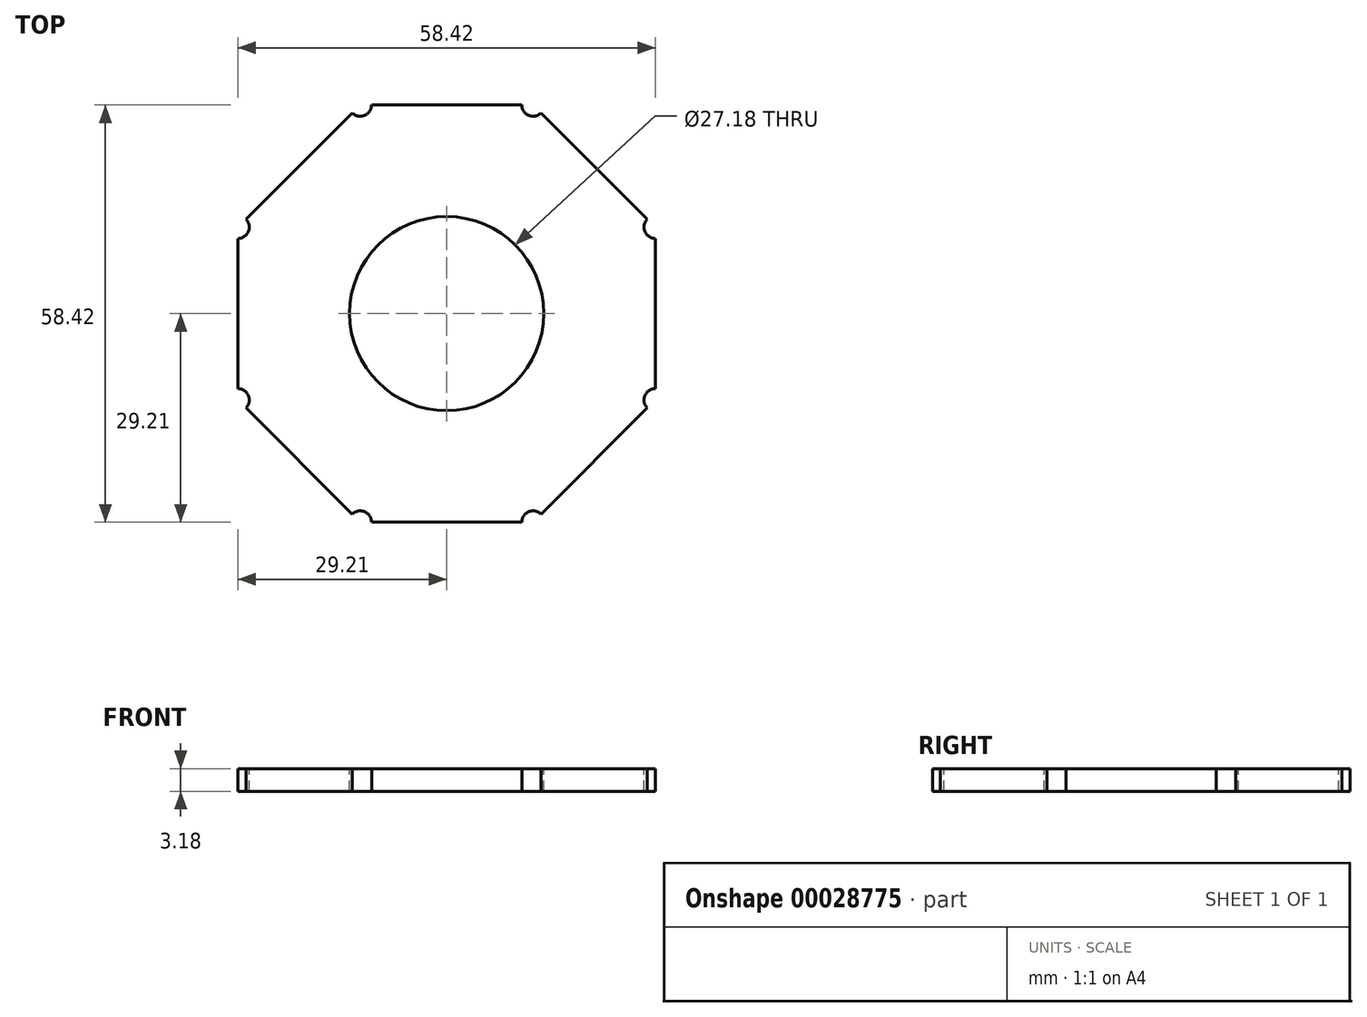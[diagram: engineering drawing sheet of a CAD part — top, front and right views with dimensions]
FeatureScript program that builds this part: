
annotation { "Feature Type Name" : "Feature", "Feature Type Description" : "" }
export const myFeature = defineFeature(function(context is Context, id is Id, definition is map)
    precondition{}
    {
        {
            var Q0;
            Q0=qCreatedBy(makeId("Top.planeOp"),FACE);
            var sketch = newSketch(context, id + "F0", { "sketchPlane" : qUnion([Q0])});
            skCircle(sketch, "E0", {"center": v(0, 0) * mm, "radius": 13.59 * mm});
            skCircle(sketch, "E1.cCircle", {"center": v(0, 0) * mm, "radius": 29.21 * mm, "construction": true});
            skLineSegment(sketch, "E1.0", {"start": v(-12.1, 29.2) * mm, "end": v(12.1, 29.2) * mm});
            skLineSegment(sketch, "E1.1", {"start": v(12.1, 29.2) * mm, "end": v(29.21, 12.1) * mm});
            skLineSegment(sketch, "E1.2", {"start": v(29.2, 12.1) * mm, "end": v(29.21, -12.1) * mm});
            skLineSegment(sketch, "E1.3", {"start": v(29.21, -12.1) * mm, "end": v(12.1, -29.2) * mm});
            skLineSegment(sketch, "E1.4", {"start": v(12.1, -29.2) * mm, "end": v(-12.1, -29.2) * mm});
            skLineSegment(sketch, "E1.5", {"start": v(-12.1, -29.21) * mm, "end": v(-29.21, -12.1) * mm});
            skLineSegment(sketch, "E1.6", {"start": v(-29.2, -12.1) * mm, "end": v(-29.2, 12.1) * mm});
            skLineSegment(sketch, "E1.7", {"start": v(-29.21, 12.1) * mm, "end": v(-12.1, 29.2) * mm});
            skPoint(sketch, "E1.0.midPoint", {"position": v(0, 29.2) * mm});
            skLineSegment(sketch, "E2", {"start": v(0, 0) * mm, "end": v(-12.1, 29.2) * mm, "construction": true});
            skLineSegment(sketch, "E3", {"start": v(0, 0) * mm, "end": v(12.1, 29.2) * mm, "construction": true});
            skLineSegment(sketch, "E4", {"start": v(0, 0) * mm, "end": v(29.21, -12.1) * mm, "construction": true});
            skLineSegment(sketch, "E5", {"start": v(0, 0) * mm, "end": v(12.1, -29.21) * mm, "construction": true});
            skLineSegment(sketch, "E6", {"start": v(0, 0) * mm, "end": v(29.2, 12.1) * mm, "construction": true});
            skLineSegment(sketch, "E7", {"start": v(0, 0) * mm, "end": v(-12.1, -29.2) * mm, "construction": true});
            skLineSegment(sketch, "E8", {"start": v(0, 0) * mm, "end": v(-29.21, -12.1) * mm});
            skLineSegment(sketch, "E9", {"start": v(0, 0) * mm, "end": v(-29.21, 12.1) * mm, "construction": true});
            skCircle(sketch, "E10", {"center": v(-12.1, 29.2) * mm, "radius": 1.59 * mm});
            skCircle(sketch, "E11", {"center": v(12.1, 29.2) * mm, "radius": 1.59 * mm});
            skCircle(sketch, "E12", {"center": v(29.2, 12.1) * mm, "radius": 1.59 * mm});
            skCircle(sketch, "E13", {"center": v(29.21, -12.1) * mm, "radius": 1.59 * mm});
            skCircle(sketch, "E14", {"center": v(12.1, -29.2) * mm, "radius": 1.59 * mm});
            skCircle(sketch, "E15", {"center": v(-12.1, -29.2) * mm, "radius": 1.59 * mm});
            skCircle(sketch, "E16", {"center": v(-29.21, -12.1) * mm, "radius": 1.59 * mm});
            skCircle(sketch, "E17", {"center": v(-29.2, 12.1) * mm, "radius": 1.59 * mm});
            skLineSegment(sketch, "E18", {"start": v(-29.21, -12.1) * mm, "end": v(-38.5, 10.35) * mm, "construction": true});
            skSolve(sketch);
        }
        {
            var Q0;
            Q0=makeQuery(id+"F0.imprint","IMPRINT",FACE,{"disambiguationData":[TD([[makeQuery(id+"F0.imprint","IMPRINT",EDGE,{"derivedFrom":sQuery(id+"F0.wireOp",EDGE,"E0")}),-1.0]])]});
            extrude(context, id + "F1", {"entities" : qUnion([Q0]), "oppositeDirection" : true, "depth" : 3.17 * mm});
        }
    });
